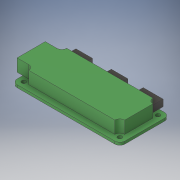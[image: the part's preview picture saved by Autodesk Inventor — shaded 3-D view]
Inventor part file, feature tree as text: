
AUTODESK INVENTOR PART (.ipt)
format: ipt  version: 2019 (Build 230136000, 136)  size: 195,584 bytes
history: native  units: mm
features: extrude x3, sketch x3
ambient origin geometry x8: Origin, YZ Plane, XZ Plane, XY Plane, X Axis, Y Axis, Z Axis, Center Point
bodies: Solid1 (feature_tree)
feature tree (6):
  extrude  "Extrusion1"  Depth=30.0mm
  extrude  "Extrusion3"  Depth=2.5mm
  extrude  "Extrusion5"  Depth=3.5mm
  sketch  "Sketch1"  dims[d0=65.0mm d1=30.0mm]
  sketch  "Sketch2"  dims[d2=3.0mm d3=2.5mm]
  sketch  "Sketch5"  dims[d4=3.5mm d5=3.5mm d6=20.0mm d8=23.0mm d9=20.0mm d11=58.0mm d14=1.6mm d15=0.0mm d17=6.0mm d18=20.0mm d20=23.0mm d21=20.0mm d23=58.0mm d28=7.0mm d29=7.0mm d30=7.5mm d31=0.0mm d37=10.0mm d38=6.0mm d39=32.628801mm d40=10.0mm d41=6.0mm d42=54.0mm d43=4.0mm d44=0.0mm d45=12.0mm d46=6.0mm d47=12.4mm]
